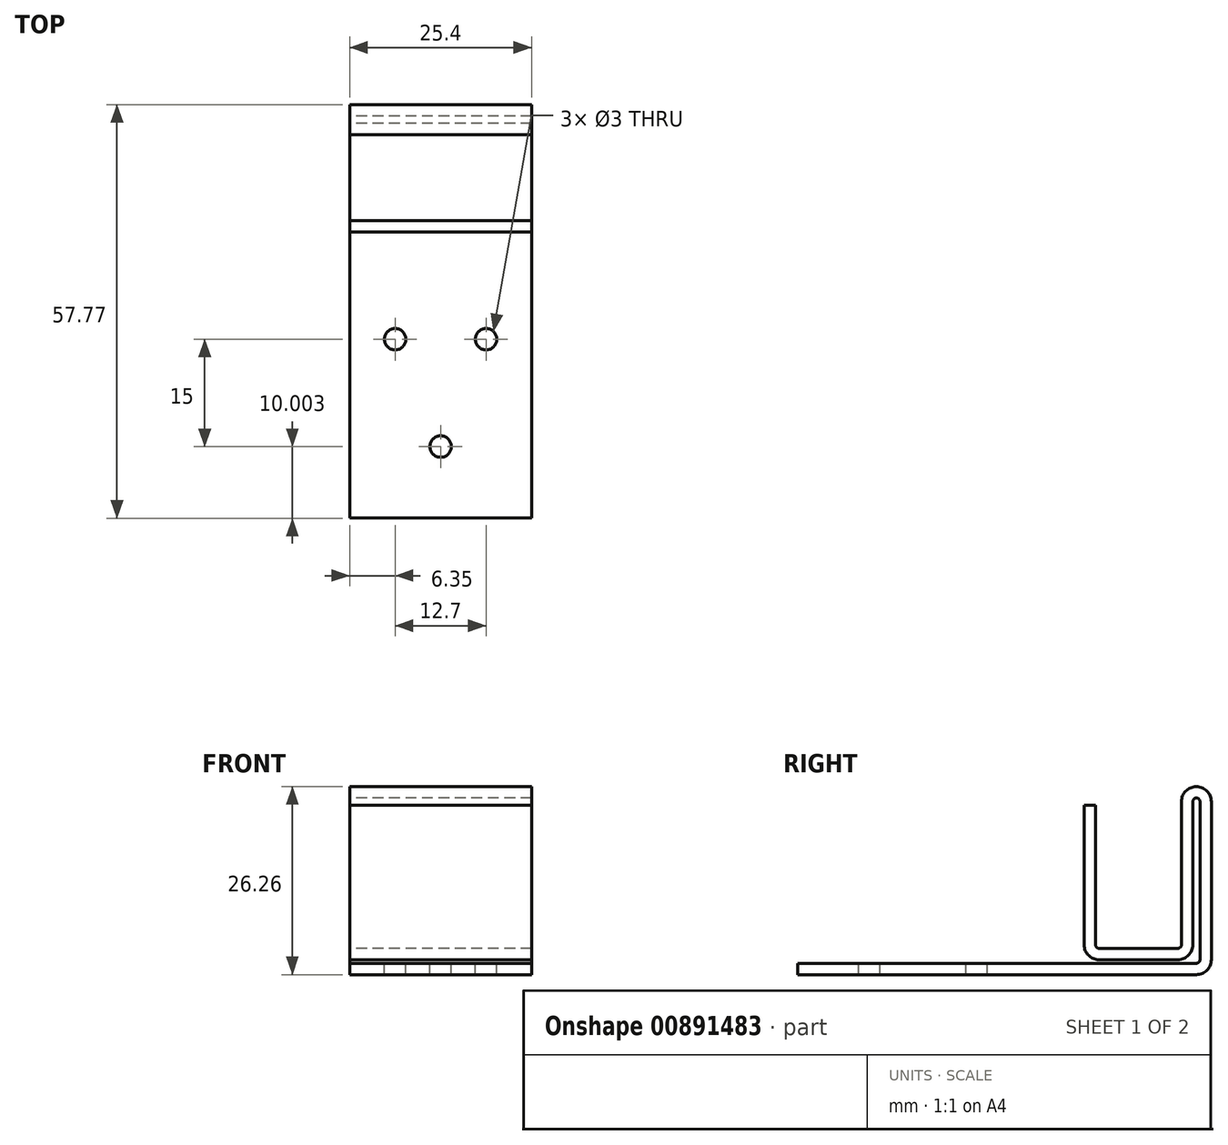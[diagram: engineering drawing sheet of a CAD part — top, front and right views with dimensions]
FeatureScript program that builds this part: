
annotation { "Feature Type Name" : "Feature", "Feature Type Description" : "" }
export const myFeature = defineFeature(function(context is Context, id is Id, definition is map)
    precondition{}
    {
        {
            var Q0;
            Q0=qCreatedBy(makeId("Right.planeOp"),FACE);
            var sketch = newSketch(context, id + "F0", { "sketchPlane" : qUnion([Q0])});
            skLineSegment(sketch, "E0.top", {"start": v(5.6, -11.49) * mm, "end": v(-5.4, -11.49) * mm});
            skLineSegment(sketch, "E0.left", {"start": v(6.1, 9.01) * mm, "end": v(6.1, -10.99) * mm});
            skLineSegment(sketch, "E0.right", {"start": v(-5.9, 8.51) * mm, "end": v(-5.9, -10.99) * mm});
            skPoint(sketch, "E0.middle", {"position": v(0, 0) * mm});
            skLineSegment(sketch, "E1.0", {"start": v(7.69, 9.01) * mm, "end": v(7.69, -10.99) * mm});
            skLineSegment(sketch, "E1.1", {"start": v(5.6, -13.07) * mm, "end": v(-5.4, -13.07) * mm});
            skLineSegment(sketch, "E1.2", {"start": v(-7.49, 8.51) * mm, "end": v(-7.49, -10.99) * mm});
            skLineSegment(sketch, "E2.0", {"start": v(8.69, 9.01) * mm, "end": v(8.69, -13.07) * mm});
            skLineSegment(sketch, "E3.0", {"start": v(10.27, 9.01) * mm, "end": v(10.27, -13.07) * mm});
            skLineSegment(sketch, "E4.0", {"start": v(8.19, -13.57) * mm, "end": v(-47.49, -13.58) * mm});
            skLineSegment(sketch, "E5.0", {"start": v(8.19, -15.16) * mm, "end": v(-47.49, -15.16) * mm});
            skLineSegment(sketch, "E6", {"start": v(-47.49, -15.16) * mm, "end": v(-47.49, -13.58) * mm});
            skLineSegment(sketch, "E7", {"start": v(-7.49, 8.51) * mm, "end": v(-5.9, 8.51) * mm});
            skArc(sketch, "E8", {"start": v(7.69, 9.01) * mm, "mid": v(8.19, 9.51) * mm, "end": v(8.69, 9.01) * mm});
            skArc(sketch, "E9", {"start": v(6.1, 9.01) * mm, "mid": v(8.19, 11.1) * mm, "end": v(10.27, 9.01) * mm});
            skPoint(sketch, "E10.visualSharp", {"position": v(6.1, -11.49) * mm});
            skArc(sketch, "E10.filletArc", {"start": v(5.6, -11.49) * mm, "mid": v(5.95, -11.34) * mm, "end": v(6.1, -10.99) * mm});
            skPoint(sketch, "E11.visualSharp", {"position": v(-5.9, -11.49) * mm});
            skArc(sketch, "E11.filletArc", {"start": v(-5.9, -10.99) * mm, "mid": v(-5.75, -11.34) * mm, "end": v(-5.4, -11.49) * mm});
            skPoint(sketch, "E12.visualSharp", {"position": v(8.69, -13.57) * mm});
            skArc(sketch, "E12.filletArc", {"start": v(8.19, -13.57) * mm, "mid": v(8.54, -13.43) * mm, "end": v(8.69, -13.07) * mm});
            skPoint(sketch, "E13.visualSharp", {"position": v(10.28, -15.16) * mm});
            skArc(sketch, "E13.filletArc", {"start": v(8.19, -15.16) * mm, "mid": v(9.66, -14.55) * mm, "end": v(10.27, -13.07) * mm});
            skPoint(sketch, "E14.visualSharp", {"position": v(-7.49, -13.08) * mm});
            skArc(sketch, "E14.filletArc", {"start": v(-7.49, -10.99) * mm, "mid": v(-6.88, -12.46) * mm, "end": v(-5.4, -13.07) * mm});
            skPoint(sketch, "E15.visualSharp", {"position": v(7.69, -13.07) * mm});
            skArc(sketch, "E15.filletArc", {"start": v(5.6, -13.07) * mm, "mid": v(7.08, -12.46) * mm, "end": v(7.69, -10.99) * mm});
            skSolve(sketch);
        }
        {
            var Q0;
            Q0=makeQuery(id+"F0.imprint","IMPRINT",FACE,{"disambiguationData":[TD([[makeQuery(id+"F0.imprint","IMPRINT",EDGE,{"derivedFrom":sQuery(id+"F0.wireOp",EDGE,"E0.top")}),1.0]])]});
            extrude(context, id + "F1", {"entities" : qUnion([Q0]), "endBound" : BoundingType.SYMMETRIC, "depth" : 25.4 * mm, "offsetDistance" : 25 * mm});
        }
        {
            var Q0;
            Q0=makeQuery(id+"F1.opExtrude","SWEPT_FACE",FACE,{"disambiguationData":[OSD([sQuery(id+"F0.wireOp",EDGE,"E4.0")])]});
            var sketch = newSketch(context, id + "F2", { "sketchPlane" : qUnion([Q0])});
            skPoint(sketch, "E16", {"position": v(-6.35, -22.49) * mm});
            skPoint(sketch, "E17", {"position": v(6.35, -22.49) * mm});
            skPoint(sketch, "E18", {"position": v(0, -37.49) * mm});
            skSolve(sketch);
        }
        {
            var Q0;
            Q0=sQuery(id+"F2.wireOp",VERTEX,"E16");
            var Q1;
            Q1=sQuery(id+"F2.wireOp",VERTEX,"E17");
            var Q2;
            Q2=sQuery(id+"F2.wireOp",VERTEX,"E18");
            var Q3;
            Q3=makeQuery(id+"F1.opExtrude","SWEPT_BODY",BODY,{"disambiguationData":[OSD([sQuery(id+"F0.wireOp",EDGE,"E0.top"),sQuery(id+"F0.wireOp",EDGE,"E0.left"),sQuery(id+"F0.wireOp",EDGE,"E0.right"),sQuery(id+"F0.wireOp",EDGE,"E1.0"),sQuery(id+"F0.wireOp",EDGE,"E1.1"),sQuery(id+"F0.wireOp",EDGE,"E1.2"),sQuery(id+"F0.wireOp",EDGE,"E2.0"),sQuery(id+"F0.wireOp",EDGE,"E3.0"),sQuery(id+"F0.wireOp",EDGE,"E4.0"),sQuery(id+"F0.wireOp",EDGE,"E5.0"),sQuery(id+"F0.wireOp",EDGE,"E6"),sQuery(id+"F0.wireOp",EDGE,"E7"),sQuery(id+"F0.wireOp",EDGE,"E8"),sQuery(id+"F0.wireOp",EDGE,"E9"),sQuery(id+"F0.wireOp",EDGE,"E10.filletArc"),sQuery(id+"F0.wireOp",EDGE,"E11.filletArc"),sQuery(id+"F0.wireOp",EDGE,"E12.filletArc"),sQuery(id+"F0.wireOp",EDGE,"E13.filletArc"),sQuery(id+"F0.wireOp",EDGE,"E14.filletArc"),sQuery(id+"F0.wireOp",EDGE,"E15.filletArc")])]});
            hole(context, id + "F3", {"style" : HoleStyle.SIMPLE, "endStyle" : HoleEndStyle.THROUGH, "holeDiameter" : 3 * mm, "majorDiameter" : 5 * mm, "isTappedThrough" : true, "tappedDepth" : 12 * mm, "tapClearance" : 3, "locations" : qUnion([Q0, Q1, Q2]), "scope" : qUnion([Q3])});
        }
    });
